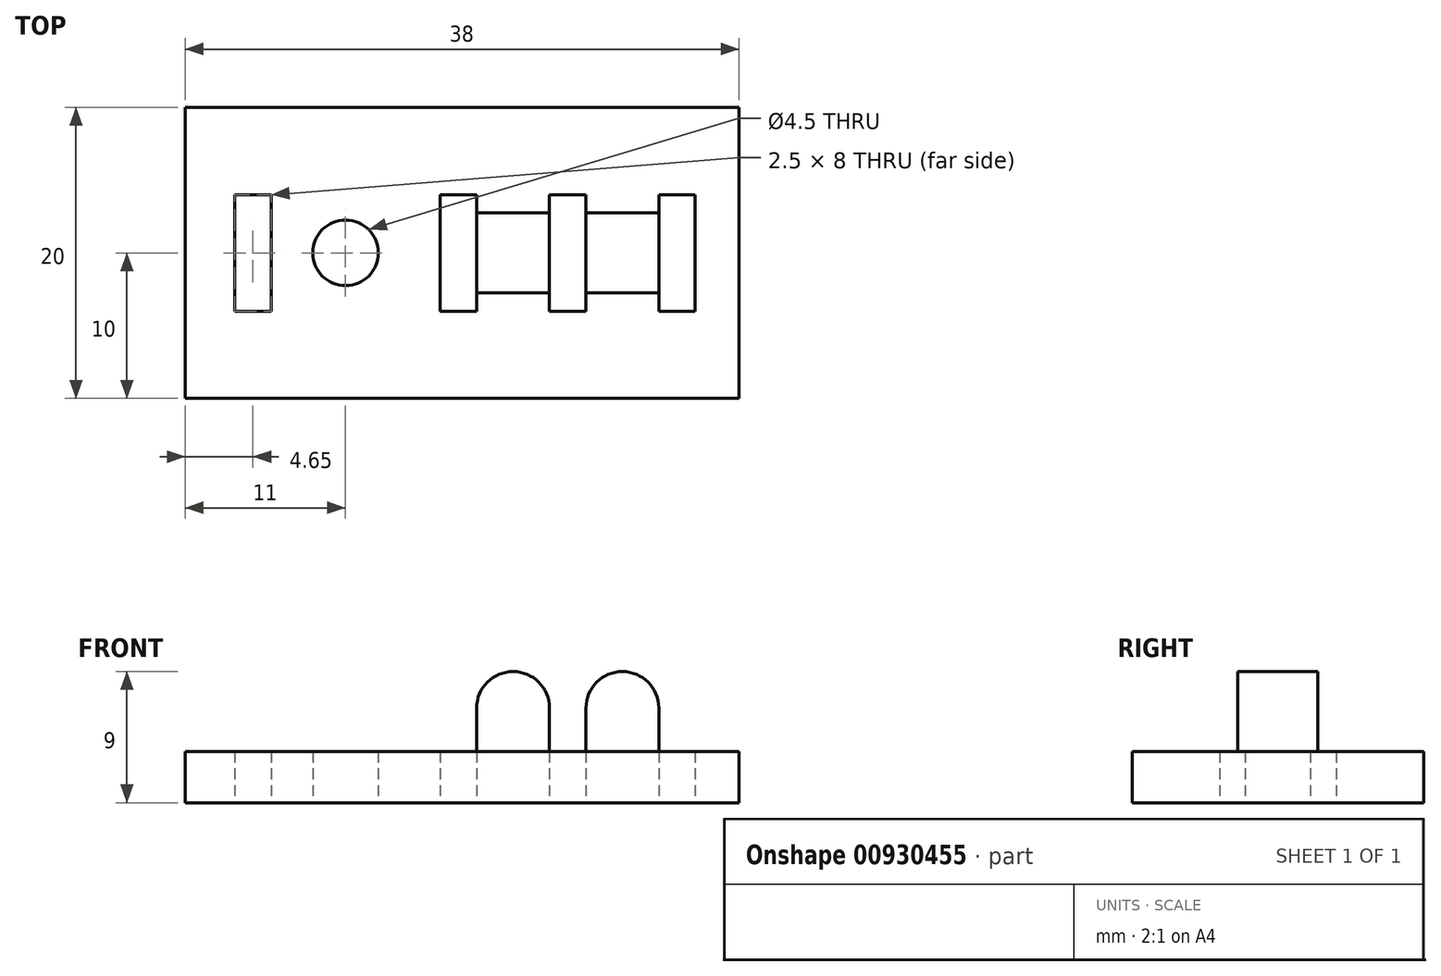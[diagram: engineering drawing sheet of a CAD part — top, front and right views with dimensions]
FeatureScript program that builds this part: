
annotation { "Feature Type Name" : "Feature", "Feature Type Description" : "" }
export const myFeature = defineFeature(function(context is Context, id is Id, definition is map)
    precondition{}
    {
        {
            var Q0;
            Q0=qCreatedBy(makeId("Top.planeOp"),FACE);
            var sketch = newSketch(context, id + "F0", { "sketchPlane" : qUnion([Q0])});
            skLineSegment(sketch, "E0.right", {"start": v(30, 0) * mm, "end": v(30, -20) * mm});
            skLineSegment(sketch, "E1", {"start": v(0, -10) * mm, "end": v(19.5, -10) * mm, "construction": true});
            skLineSegment(sketch, "E2.0", {"start": v(17, -6) * mm, "end": v(17, -14) * mm});
            skLineSegment(sketch, "E3.0", {"start": v(12, -6) * mm, "end": v(12, -14) * mm});
            skLineSegment(sketch, "E4", {"start": v(30, 0) * mm, "end": v(-8, 0) * mm});
            skLineSegment(sketch, "E5", {"start": v(30, -20) * mm, "end": v(-8, -20) * mm});
            skLineSegment(sketch, "E6.0", {"start": v(3, 0) * mm, "end": v(3, -20) * mm, "construction": true});
            skCircle(sketch, "E7", {"center": v(3, -10) * mm, "radius": 2.25 * mm});
            skPoint(sketch, "E8.orphan", {"position": v(108.7, -6.5) * mm});
            skPoint(sketch, "E9.orphan", {"position": v(108.7, -13.5) * mm});
            skPoint(sketch, "E10.orphan", {"position": v(10.5, 0) * mm});
            skPoint(sketch, "E11.0.start.orphan", {"position": v(0, -6.5) * mm});
            skPoint(sketch, "E12.orphan", {"position": v(0, -13.5) * mm});
            skLineSegment(sketch, "E13.0", {"start": v(-2.1, -6) * mm, "end": v(-2.1, -14) * mm});
            skLineSegment(sketch, "E14.0", {"start": v(-8, 0) * mm, "end": v(-8, -20) * mm});
            skLineSegment(sketch, "E15.0", {"start": v(-4.6, -6) * mm, "end": v(-4.6, -14) * mm});
            skLineSegment(sketch, "E16.0", {"start": v(9.5, -6) * mm, "end": v(9.5, -14) * mm});
            skLineSegment(sketch, "E17.0", {"start": v(19.5, -6) * mm, "end": v(19.5, -14) * mm});
            skPoint(sketch, "E18.orphan", {"position": v(-5, 0) * mm});
            skLineSegment(sketch, "E19.bottom", {"start": v(24.5, -10) * mm, "end": v(25, -10) * mm});
            skLineSegment(sketch, "E19.top", {"start": v(-4.6, -6) * mm, "end": v(-2.1, -6) * mm});
            skLineSegment(sketch, "E20.MirrorCS", {"start": v(-4.6, -14) * mm, "end": v(-2.1, -14) * mm});
            skPoint(sketch, "E21.orphan", {"position": v(22.5, -14) * mm});
            skLineSegment(sketch, "E22.0", {"start": v(24.5, -6) * mm, "end": v(24.5, -14) * mm});
            skLineSegment(sketch, "E23.0", {"start": v(27, -6) * mm, "end": v(27, -14) * mm});
            skPoint(sketch, "E24.orphan", {"position": v(25, -14) * mm});
            skPoint(sketch, "E19.right.end.orphan", {"position": v(25, -6) * mm});
            skPoint(sketch, "E25.MirrorCS.start.orphan", {"position": v(25, -10) * mm});
            skLineSegment(sketch, "E26.trimOffspring", {"start": v(27, -10) * mm, "end": v(108.7, -10) * mm, "construction": true});
            skLineSegment(sketch, "E27.trimOffspring", {"start": v(9.5, -14) * mm, "end": v(12, -14) * mm});
            skLineSegment(sketch, "E28.trimOffspring", {"start": v(9.5, -6) * mm, "end": v(12, -6) * mm});
            skLineSegment(sketch, "E29.trimOffspring", {"start": v(17, -6) * mm, "end": v(19.5, -6) * mm});
            skLineSegment(sketch, "E30.trimOffspring", {"start": v(17, -14) * mm, "end": v(19.5, -14) * mm});
            skLineSegment(sketch, "E31.trimOffspring", {"start": v(24.5, -6) * mm, "end": v(27, -6) * mm});
            skLineSegment(sketch, "E32.trimOffspring", {"start": v(24.5, -14) * mm, "end": v(27, -14) * mm});
            skSolve(sketch);
        }
        {
            var Q0;
            Q0=makeQuery(id+"F0.imprint","IMPRINT",FACE,{"disambiguationData":[TD([[makeQuery(id+"F0.imprint","IMPRINT",EDGE,{"derivedFrom":sQuery(id+"F0.wireOp",EDGE,"E0.right")}),-1.0]])]});
            extrude(context, id + "F1", {"entities" : qUnion([Q0]), "depth" : 3.5 * mm, "offsetDistance" : 25 * mm});
        }
        {
            var Q0;
            Q0=makeQuery(id+"F1.opExtrude","CAP_FACE",FACE,{"disambiguationData":[OSD([sQuery(id+"F0.wireOp",EDGE,"E0.right"),sQuery(id+"F0.wireOp",EDGE,"E2.0"),sQuery(id+"F0.wireOp",EDGE,"E3.0"),sQuery(id+"F0.wireOp",EDGE,"E4"),sQuery(id+"F0.wireOp",EDGE,"E5"),sQuery(id+"F0.wireOp",EDGE,"E7"),sQuery(id+"F0.wireOp",EDGE,"E13.0"),sQuery(id+"F0.wireOp",EDGE,"E14.0"),sQuery(id+"F0.wireOp",EDGE,"E15.0"),sQuery(id+"F0.wireOp",EDGE,"E16.0"),sQuery(id+"F0.wireOp",EDGE,"E17.0"),sQuery(id+"F0.wireOp",EDGE,"E19.top"),sQuery(id+"F0.wireOp",EDGE,"E20.MirrorCS"),sQuery(id+"F0.wireOp",EDGE,"E22.0"),sQuery(id+"F0.wireOp",EDGE,"E23.0"),sQuery(id+"F0.wireOp",EDGE,"E27.trimOffspring"),sQuery(id+"F0.wireOp",EDGE,"E28.trimOffspring"),sQuery(id+"F0.wireOp",EDGE,"E29.trimOffspring"),sQuery(id+"F0.wireOp",EDGE,"E30.trimOffspring"),sQuery(id+"F0.wireOp",EDGE,"E31.trimOffspring"),sQuery(id+"F0.wireOp",EDGE,"E32.trimOffspring")])],"isStart":false});
            var sketch = newSketch(context, id + "F2", { "sketchPlane" : qUnion([Q0])});
            skLineSegment(sketch, "E33.left", {"start": v(19.5, -7.25) * mm, "end": v(19.5, -12.75) * mm});
            skLineSegment(sketch, "E33.right", {"start": v(24.5, -7.25) * mm, "end": v(24.5, -12.75) * mm});
            skLineSegment(sketch, "E34.left", {"start": v(17, -7.25) * mm, "end": v(17, -12.75) * mm});
            skLineSegment(sketch, "E34.right", {"start": v(12, -7.25) * mm, "end": v(12, -12.75) * mm});
            skLineSegment(sketch, "E35.0", {"start": v(12, -12.75) * mm, "end": v(17, -12.75) * mm});
            skLineSegment(sketch, "E36.0", {"start": v(12, -7.25) * mm, "end": v(17, -7.25) * mm});
            skLineSegment(sketch, "E37.trimOffspring", {"start": v(19.5, -7.25) * mm, "end": v(24.5, -7.25) * mm});
            skLineSegment(sketch, "E38.trimOffspring", {"start": v(19.5, -12.75) * mm, "end": v(24.5, -12.75) * mm});
            skPoint(sketch, "E34.bottom.start.orphan", {"position": v(17, -6.5) * mm});
            skPoint(sketch, "E33.bottom.start.orphan", {"position": v(19.5, -6.5) * mm});
            skPoint(sketch, "E39.start.orphan", {"position": v(12, -10) * mm});
            skSolve(sketch);
        }
        {
            var Q0;
            Q0=makeQuery(id+"F2.imprint","IMPRINT",FACE,{"disambiguationData":[TD([[makeQuery(id+"F2.imprint","IMPRINT",EDGE,{"derivedFrom":sQuery(id+"F2.wireOp",EDGE,"E33.left")}),1.0]])]});
            var Q1;
            Q1=makeQuery(id+"F2.imprint","IMPRINT",FACE,{"disambiguationData":[TD([[makeQuery(id+"F2.imprint","IMPRINT",EDGE,{"derivedFrom":sQuery(id+"F2.wireOp",EDGE,"E34.left")}),-1.0]])]});
            extrude(context, id + "F3", {"entities" : qUnion([Q0, Q1]), "operationType" : NewBodyOperationType.ADD, "depth" : 5.5 * mm, "offsetDistance" : 25 * mm});
        }
        {
            var Q0;
            Q0=makeQuery(id+"F3.opExtrude","CAP_EDGE",EDGE,{"disambiguationData":[OSD([sQuery(id+"F2.wireOp",EDGE,"E34.right")])],"isStart":false});
            var Q1;
            Q1=makeQuery(id+"F3.opExtrude","CAP_EDGE",EDGE,{"disambiguationData":[OSD([sQuery(id+"F2.wireOp",EDGE,"E34.left")])],"isStart":false});
            var Q2;
            Q2=makeQuery(id+"F3.opExtrude","CAP_EDGE",EDGE,{"disambiguationData":[OSD([sQuery(id+"F2.wireOp",EDGE,"E33.left")])],"isStart":false});
            var Q3;
            Q3=makeQuery(id+"F3.opExtrude","CAP_EDGE",EDGE,{"disambiguationData":[OSD([sQuery(id+"F2.wireOp",EDGE,"E33.right")])],"isStart":false});
            fillet(context, id + "F4", {"entities" : qUnion([Q0, Q1, Q2, Q3]), "radius" : 2.5 * mm, "tangentPropagation" : true, "allowEdgeOverflow" : false});
        }
    });
